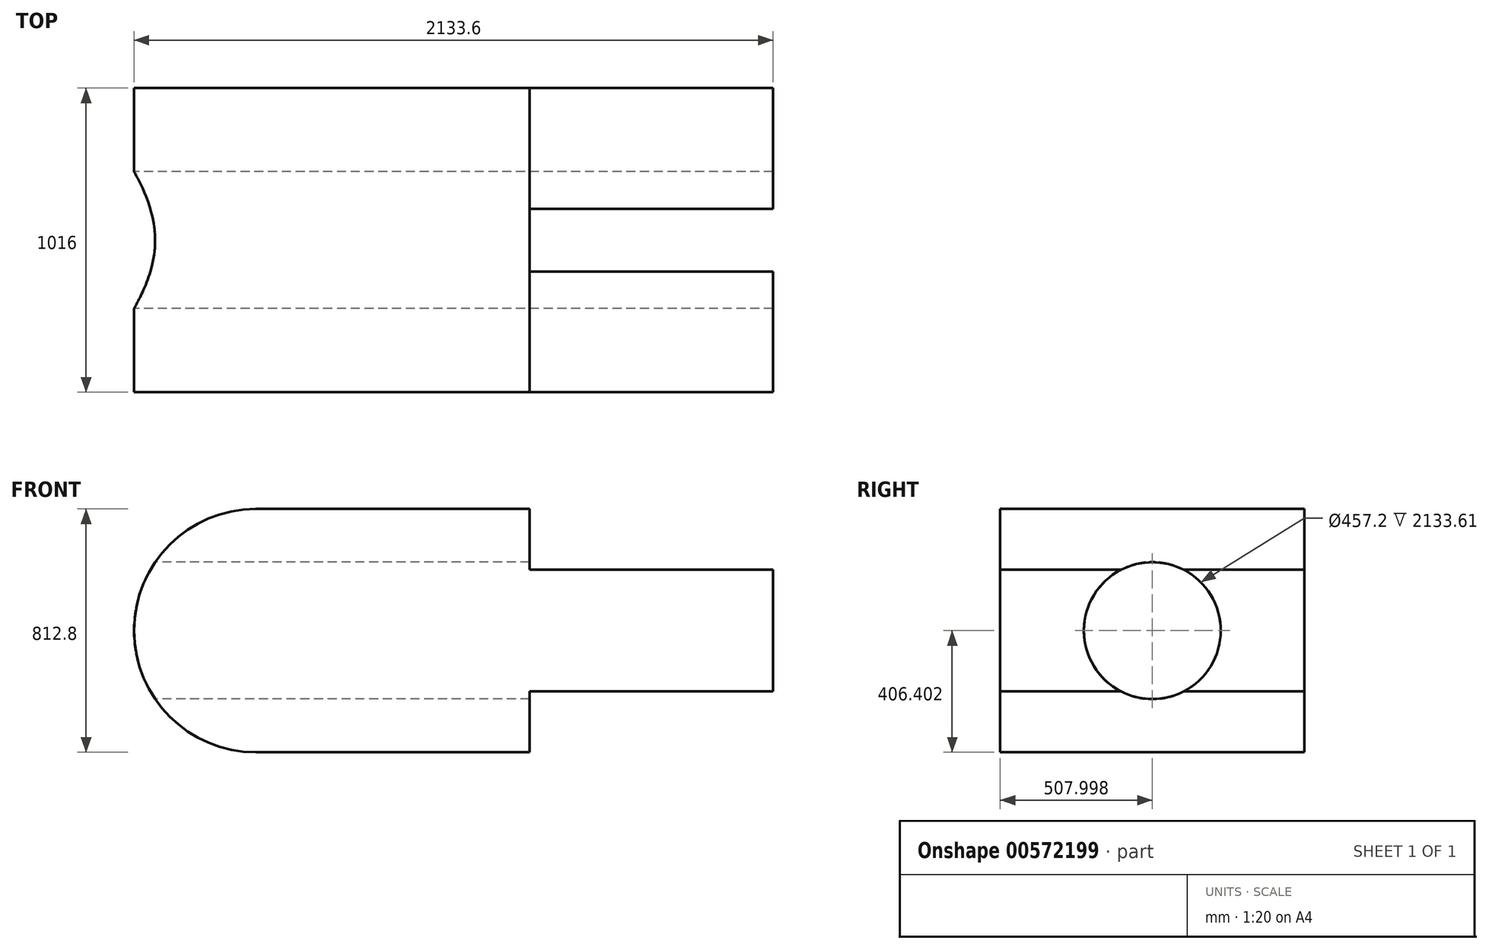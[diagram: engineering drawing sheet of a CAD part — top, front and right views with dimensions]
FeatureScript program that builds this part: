
annotation { "Feature Type Name" : "Feature", "Feature Type Description" : "" }
export const myFeature = defineFeature(function(context is Context, id is Id, definition is map)
    precondition{}
    {
        {
            var Q0;
            Q0=qCreatedBy(makeId("Right.planeOp"),FACE);
            var sketch = newSketch(context, id + "F0", { "sketchPlane" : qUnion([Q0])});
            skLineSegment(sketch, "E0", {"start": v(-75.58, -75.25) * mm, "end": v(940.42, -75.25) * mm});
            skLineSegment(sketch, "E1", {"start": v(940.42, -75.25) * mm, "end": v(940.42, 737.55) * mm});
            skLineSegment(sketch, "E2", {"start": v(940.42, 737.55) * mm, "end": v(-75.58, 737.55) * mm});
            skLineSegment(sketch, "E3", {"start": v(-75.58, 737.55) * mm, "end": v(-75.58, -75.25) * mm});
            skCircle(sketch, "E4", {"center": v(432.42, 331.15) * mm, "radius": 228.6 * mm});
            skPoint(sketch, "E4.centerSnap0", {"position": v(-75.58, 331.15) * mm});
            skPoint(sketch, "E4.centerSnap1", {"position": v(432.42, -75.25) * mm});
            skSolve(sketch);
        }
        {
            var Q0;
            Q0=makeQuery(id+"F0.imprint","IMPRINT",FACE,{"disambiguationData":[TD([[makeQuery(id+"F0.imprint","IMPRINT",EDGE,{"derivedFrom":sQuery(id+"F0.wireOp",EDGE,"E0")}),1.0]])]});
            extrude(context, id + "F1", {"entities" : qUnion([Q0]), "depth" : 2133.6 * mm, "offsetDistance" : 25.4 * mm});
        }
        {
            var Q0;
            Q0=makeQuery(id+"F1.opExtrude","SWEPT_FACE",FACE,{"disambiguationData":[OSD([sQuery(id+"F0.wireOp",EDGE,"E3")])]});
            var sketch = newSketch(context, id + "F2", { "sketchPlane" : qUnion([Q0])});
            skLineSegment(sketch, "E5", {"start": v(0, -75.25) * mm, "end": v(0, 331.15) * mm});
            skLineSegment(sketch, "E6", {"start": v(0, 331.15) * mm, "end": v(203.2, 331.15) * mm});
            skLineSegment(sketch, "E7", {"start": v(406.4, 127.95) * mm, "end": v(406.4, -75.25) * mm});
            skLineSegment(sketch, "E8", {"start": v(406.4, -75.25) * mm, "end": v(1320.8, -75.25) * mm});
            skLineSegment(sketch, "E9", {"start": v(1320.8, -75.25) * mm, "end": v(2133.6, -75.25) * mm});
            skCircle(sketch, "E10", {"center": v(406.4, 331.15) * mm, "radius": 203.2 * mm});
            skArc(sketch, "E11", {"start": v(406.4, 737.55) * mm, "mid": v(0, 331.15) * mm, "end": v(406.4, -75.25) * mm});
            skPoint(sketch, "E11.third.point", {"position": v(406.4, 737.55) * mm});
            skLineSegment(sketch, "E12", {"start": v(1320.8, -75.25) * mm, "end": v(1320.8, 127.95) * mm});
            skLineSegment(sketch, "E13", {"start": v(1320.8, 127.95) * mm, "end": v(2133.6, 127.95) * mm});
            skLineSegment(sketch, "E14", {"start": v(2133.6, 127.95) * mm, "end": v(2133.6, 534.35) * mm});
            skLineSegment(sketch, "E15", {"start": v(2133.6, 534.35) * mm, "end": v(1320.8, 534.35) * mm});
            skLineSegment(sketch, "E16", {"start": v(1320.8, 534.35) * mm, "end": v(1320.8, 737.55) * mm});
            skLineSegment(sketch, "E17", {"start": v(1320.8, 737.55) * mm, "end": v(406.4, 737.55) * mm});
            skSolve(sketch);
        }
        {
            var Q0;
            {var subQ1=sQuery(id+"F0.wireOp",EDGE,"E3");var subQ2=makeQuery(id+"F1.opExtrude","CAP_EDGE",EDGE,{"disambiguationData":[OSD([subQ1])],"isStart":true});var subQ4=makeQuery(id+"F1.opExtrude","SWEPT_EDGE",EDGE,{"disambiguationData":[OSD([sQuery(id+"F0.wireOp",EDGE,"E2"),subQ1])]});var subQ6=makeQuery(id+"F2.imprint","INTERSECT",VERTEX,{"derivedFrom":[subQ4,subQ2]});Q0=makeQuery(id+"F2.imprint","IMPRINT",FACE,{"disambiguationData":[TD([[makeQuery(id+"F2.imprint","IMPRINT",EDGE,{"disambiguationData":[TD([[subQ6,-1.0]])],"derivedFrom":subQ2}),1.0]])]});}
            var Q1;
            {var subQ0=sQuery(id+"F2.wireOp",EDGE,"E5");Q1=makeQuery(id+"F2.imprint","IMPRINT",FACE,{"disambiguationData":[TD([[makeQuery(id+"F2.imprint","IMPRINT",EDGE,{"derivedFrom":subQ0}),1.0]])]});}
            var Q2;
            {var subQ0=sQuery(id+"F2.wireOp",EDGE,"E9");Q2=makeQuery(id+"F2.imprint","IMPRINT",FACE,{"disambiguationData":[TD([[makeQuery(id+"F2.imprint","IMPRINT",EDGE,{"derivedFrom":subQ0}),-1.0]])]});}
            var Q3;
            {var subQ0=sQuery(id+"F2.wireOp",EDGE,"E15");Q3=makeQuery(id+"F2.imprint","IMPRINT",FACE,{"disambiguationData":[TD([[makeQuery(id+"F2.imprint","IMPRINT",EDGE,{"derivedFrom":subQ0}),-1.0]])]});}
            extrude(context, id + "F3", {"entities" : qUnion([Q0, Q1, Q2, Q3]), "operationType" : NewBodyOperationType.REMOVE, "endBound" : BoundingType.THROUGH_ALL, "oppositeDirection" : true, "depth" : 25.4 * mm, "offsetDistance" : 25.4 * mm});
        }
    });
